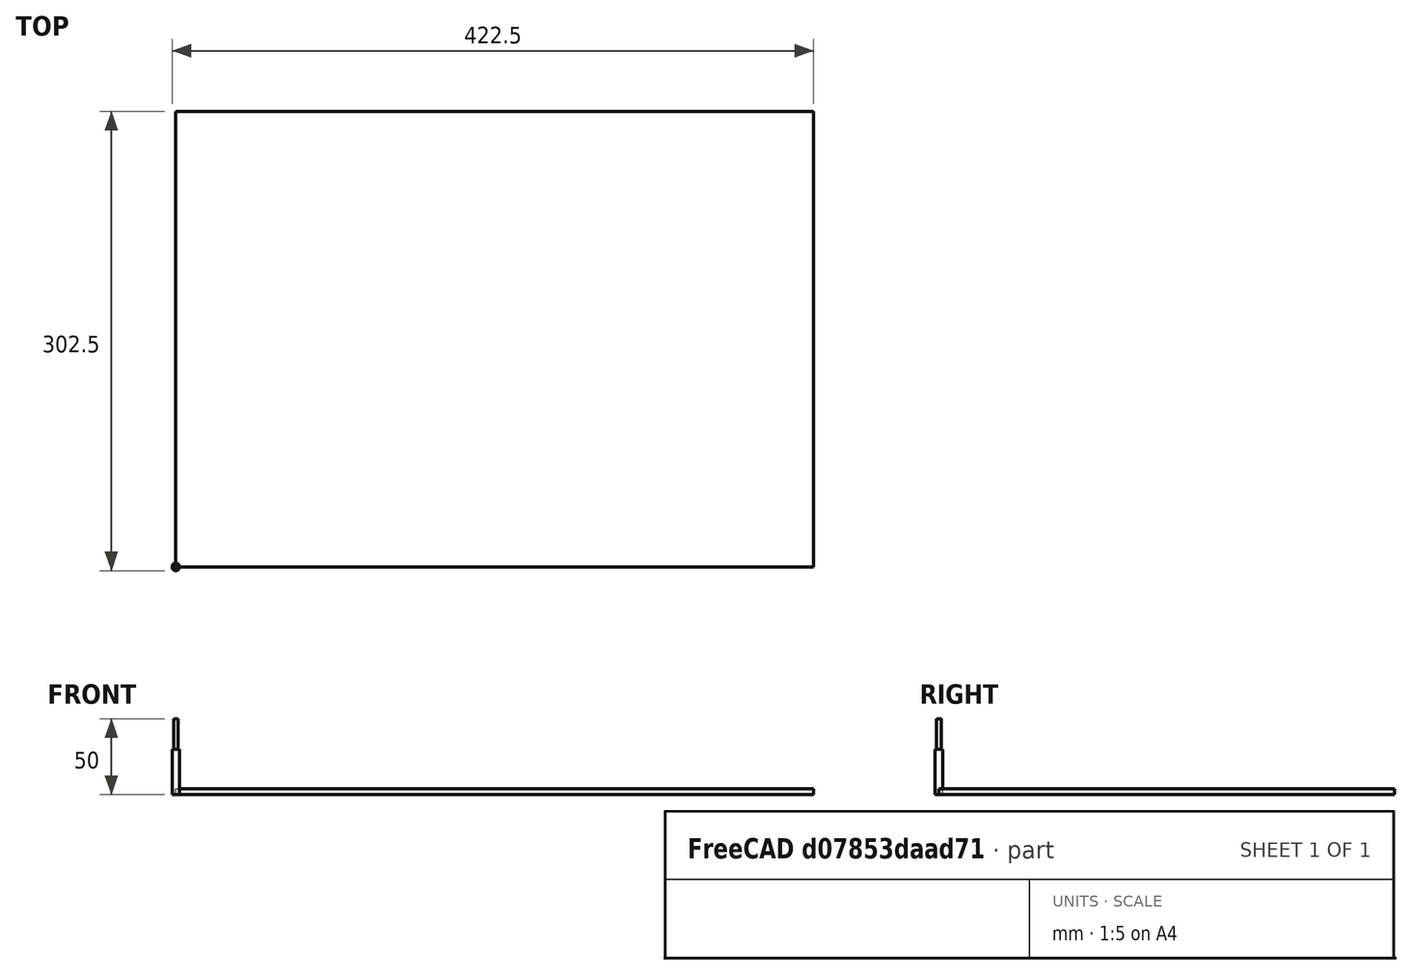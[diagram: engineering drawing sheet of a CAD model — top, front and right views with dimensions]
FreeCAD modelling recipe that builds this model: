
FCSTD DOCUMENT  (FreeCAD 1.0R39109 (Git))
Label: HousingAtari_T03.00
License: All rights reserved
LicenseURL: https://en.wikipedia.org/wiki/All_rights_reserved
objects: Sketcher::SketchObject×7, Part::Part2DObjectPython×5, Path::FeaturePython×3, App::DocumentObjectGroup×3, Part::FeaturePython×2, PartDesign::Body×1, App::FeaturePython×1, Mesh::FeaturePython×1
note: 22 computed .brp shape members not serialized (recipe doc carries the construction recipe); baked Part::Feature solids carry a one-line shape summary decoded from their .brp

FEATURE [Sketcher::SketchObject] Sketch  label="A3"
  ArcFitTolerance = 0
  FullyConstrained = false
  MakeInternals = false
  MapMode = 5
  sketch-geometry (7):
    g0: LineSegment StartX=0 StartY=420 StartZ=0 EndX=0 EndY=0 EndZ=0
    g1: LineSegment StartX=0 StartY=420 StartZ=0 EndX=148.5 EndY=420 EndZ=0
    g2: LineSegment StartX=148.5 StartY=420 StartZ=0 EndX=148.5 EndY=0 EndZ=0
    g3: LineSegment StartX=148.5 StartY=420 StartZ=0 EndX=297 EndY=420 EndZ=0
    g4: LineSegment StartX=297 StartY=420 StartZ=0 EndX=297 EndY=210 EndZ=0
    g5: LineSegment StartX=297 StartY=210 StartZ=0 EndX=297 EndY=0 EndZ=0
    g6: LineSegment StartX=297 StartY=210 StartZ=0 EndX=0 EndY=210 EndZ=0
  constraints (21):
    c: Vertical(g0)
    c: DistanceY(g0,g0) = 420
    c: Coincident(g1,g0)
    c: Horizontal(g1)
    c: Coincident(g2,g1)
    c: Coincident(g3,g1)
    c: Horizontal(g3)
    c: Equal(g1,g3)
    c: Vertical(g2)
    c: DistanceX(g0,g3) = 297
    c: Coincident(g4,g3)
    c: Vertical(g4)
    c: Coincident(g5,g4)
    c: PointOnObject(g5,g-1)
    c: Vertical(g5)
    c: Equal(g5,g4)
    c: PointOnObject(g0,g-1)
    c: PointOnObject(g0,g-2)
    c: Coincident(g6,g4)
    c: PointOnObject(g6,g0)
    c: Horizontal(g6)
FEATURE [Sketcher::SketchObject] Sketch001  label="BOX-OUTLINE"
  ArcFitTolerance = 0
  ExternalGeometry = -> [Sketch]
  FullyConstrained = false
  MakeInternals = false
  MapMode = 5
  sketch-geometry (60):
    g0: LineSegment StartX=83.5 StartY=362.836 StartZ=0 EndX=83.5 EndY=292.836 EndZ=0
    g1: LineSegment StartX=83.5 StartY=292.836 StartZ=0 EndX=83.5 EndY=222.836 EndZ=0
    g2: LineSegment StartX=83.5 StartY=222.836 StartZ=0 EndX=148.5 EndY=222.836 EndZ=0
    g3: LineSegment StartX=148.5 StartY=222.836 StartZ=0 EndX=213.5 EndY=222.836 EndZ=0
    g4: LineSegment StartX=213.5 StartY=222.836 StartZ=0 EndX=213.5 EndY=292.836 EndZ=0
    g5: LineSegment StartX=213.5 StartY=292.836 StartZ=0 EndX=213.5 EndY=362.836 EndZ=0
    g6: LineSegment StartX=213.5 StartY=362.836 StartZ=0 EndX=148.5 EndY=362.836 EndZ=0
    g7: LineSegment StartX=148.5 StartY=362.836 StartZ=0 EndX=83.5 EndY=362.836 EndZ=0
    g8: LineSegment StartX=83.5 StartY=222.836 StartZ=0 EndX=83.5 EndY=218.836 EndZ=0
    g9: LineSegment StartX=83.5 StartY=218.836 StartZ=0 EndX=213.5 EndY=218.836 EndZ=0
    g10: LineSegment StartX=213.5 StartY=218.836 StartZ=0 EndX=213.5 EndY=222.836 EndZ=0
    g11: LineSegment StartX=213.5 StartY=222.836 StartZ=0 EndX=217.5 EndY=222.836 EndZ=0
    g12: LineSegment StartX=217.5 StartY=222.836 StartZ=0 EndX=217.5 EndY=362.836 EndZ=0
    g13: LineSegment StartX=217.5 StartY=362.836 StartZ=0 EndX=213.5 EndY=362.836 EndZ=0
    g14: LineSegment StartX=213.5 StartY=362.836 StartZ=0 EndX=213.5 EndY=366.836 EndZ=0
    g15: LineSegment StartX=213.5 StartY=366.836 StartZ=0 EndX=83.5 EndY=366.836 EndZ=0
    g16: LineSegment StartX=83.5 StartY=366.836 StartZ=0 EndX=83.5 EndY=362.836 EndZ=0
    g17: LineSegment StartX=83.5 StartY=222.836 StartZ=0 EndX=79.5 EndY=222.836 EndZ=0
    g18: LineSegment StartX=79.5 StartY=222.836 StartZ=0 EndX=79.5 EndY=362.836 EndZ=0
    g19: LineSegment StartX=79.5 StartY=362.836 StartZ=0 EndX=83.5 EndY=362.836 EndZ=0
    g20: LineSegment StartX=83.5 StartY=218.836 StartZ=0 EndX=83.5 EndY=188.836 EndZ=0
    g21: LineSegment StartX=83.5 StartY=188.836 StartZ=0 EndX=213.5 EndY=188.836 EndZ=0
    g22: LineSegment StartX=213.5 StartY=188.836 StartZ=0 EndX=213.5 EndY=218.836 EndZ=0
    g23: LineSegment StartX=217.5 StartY=222.836 StartZ=0 EndX=243.5 EndY=222.836 EndZ=0
    g24: LineSegment StartX=243.5 StartY=222.836 StartZ=0 EndX=243.5 EndY=362.836 EndZ=0
    g25: LineSegment StartX=243.5 StartY=362.836 StartZ=0 EndX=217.5 EndY=362.836 EndZ=0
    g26: LineSegment StartX=213.5 StartY=366.836 StartZ=0 EndX=213.5 EndY=396.836 EndZ=0
    g27: LineSegment StartX=213.5 StartY=396.836 StartZ=0 EndX=83.5 EndY=396.836 EndZ=0
    g28: LineSegment StartX=83.5 StartY=396.836 StartZ=0 EndX=83.5 EndY=366.836 EndZ=0
    g29: LineSegment StartX=79.5 StartY=362.836 StartZ=0 EndX=53.5 EndY=362.836 EndZ=0
    g30: LineSegment StartX=53.5 StartY=362.836 StartZ=0 EndX=53.5 EndY=222.836 EndZ=0
    g31: LineSegment StartX=53.5 StartY=222.836 StartZ=0 EndX=79.5 EndY=222.836 EndZ=0
    g32: LineSegment StartX=213.5 StartY=188.836 StartZ=0 EndX=217.5 EndY=188.836 EndZ=0
    g33: LineSegment StartX=217.5 StartY=188.836 StartZ=0 EndX=217.5 EndY=222.836 EndZ=0
    g34: LineSegment StartX=213.5 StartY=218.836 StartZ=0 EndX=243.5 EndY=218.836 EndZ=0
    g35: LineSegment StartX=243.5 StartY=218.836 StartZ=0 EndX=243.5 EndY=222.836 EndZ=0
    g36: LineSegment StartX=213.5 StartY=366.836 StartZ=0 EndX=243.5 EndY=366.836 EndZ=0
    g37: LineSegment StartX=243.5 StartY=366.836 StartZ=0 EndX=243.5 EndY=362.836 EndZ=0
    g38: LineSegment StartX=217.5 StartY=362.836 StartZ=0 EndX=217.5 EndY=396.836 EndZ=0
    g39: LineSegment StartX=217.5 StartY=396.836 StartZ=0 EndX=213.5 EndY=396.836 EndZ=0
    g40: LineSegment StartX=83.5 StartY=396.836 StartZ=0 EndX=79.5 EndY=396.836 EndZ=0
    g41: LineSegment StartX=79.5 StartY=396.836 StartZ=0 EndX=79.5 EndY=362.836 EndZ=0
    g42: LineSegment StartX=53.5 StartY=362.836 StartZ=0 EndX=53.5 EndY=366.836 EndZ=0
    g43: LineSegment StartX=53.5 StartY=366.836 StartZ=0 EndX=83.5 EndY=366.836 EndZ=0
    g44: LineSegment StartX=53.5 StartY=222.836 StartZ=0 EndX=53.5 EndY=218.836 EndZ=0
    g45: LineSegment StartX=53.5 StartY=218.836 StartZ=0 EndX=83.5 EndY=218.836 EndZ=0
    g46: LineSegment StartX=79.5 StartY=222.836 StartZ=0 EndX=79.5 EndY=188.836 EndZ=0
    g47: LineSegment StartX=79.5 StartY=188.836 StartZ=0 EndX=83.5 EndY=188.836 EndZ=0
    g48: LineSegment StartX=83.5 StartY=188.836 StartZ=0 EndX=83.5 EndY=44.8363 EndZ=0
    g49: LineSegment StartX=83.5 StartY=44.8363 StartZ=0 EndX=213.5 EndY=44.8363 EndZ=0
    g50: LineSegment StartX=213.5 StartY=44.8363 StartZ=0 EndX=213.5 EndY=188.836 EndZ=0
    g51: LineSegment StartX=79.5 StartY=188.836 StartZ=0 EndX=79.5 EndY=48.8363 EndZ=0
    g52: LineSegment StartX=79.5 StartY=48.8363 StartZ=0 EndX=217.5 EndY=48.8363 EndZ=0
    g53: LineSegment StartX=217.5 StartY=48.8363 StartZ=0 EndX=217.5 EndY=188.836 EndZ=0
    g54: LineSegment StartX=79.5 StartY=192.836 StartZ=0 EndX=217.5 EndY=192.836 EndZ=0
    g55: LineSegment StartX=79.5 StartY=48.8363 StartZ=0 EndX=79.5 EndY=44.8363 EndZ=0
    g56: LineSegment StartX=217.5 StartY=48.8363 StartZ=0 EndX=217.5 EndY=44.8363 EndZ=0
    g57: LineSegment StartX=79.5 StartY=392.836 StartZ=0 EndX=217.5 EndY=392.836 EndZ=0
    g58: LineSegment StartX=247.5 StartY=366.836 StartZ=0 EndX=247.5 EndY=218.836 EndZ=0
    g59: LineSegment StartX=49.5 StartY=366.836 StartZ=0 EndX=49.5 EndY=218.836 EndZ=0
  constraints (166):
    c: Vertical(g0)
    c: Coincident(g1,g0)
    c: Vertical(g1)
    c: Coincident(g2,g1)
    c: Horizontal(g2)
    c: Coincident(g3,g2)
    c: Horizontal(g3)
    c: Coincident(g4,g3)
    c: Vertical(g4)
    c: Coincident(g5,g4)
    c: Vertical(g5)
    c: Horizontal(g6)
    c: Coincident(g7,g6)
    c: Coincident(g7,g0)
    c: Horizontal(g7)
    c: Vertical(g2,g6)
    c: Horizontal(g0,g4)
    c: Equal(g4,g5)
    c: Equal(g7,g6)
    c: Coincident(g5,g6)
    c: DistanceY(g1,g0) = 140
    c: DistanceX(g0,g5) = 130
    c: Coincident(g8,g1)
    c: Vertical(g8)
    c: Coincident(g9,g8)
    c: Horizontal(g9)
    c: Coincident(g10,g9)
    c: Coincident(g10,g3)
    c: Vertical(g10)
    c: Coincident(g11,g3)
    c: Horizontal(g11)
    c: Coincident(g12,g11)
    c: Vertical(g12)
    c: Coincident(g13,g12)
    c: Coincident(g13,g5)
    c: Horizontal(g13)
    c: Equal(g10,g11)
    c: DistanceY(g10,g10) = 4
    c: Coincident(g14,g5)
    c: Vertical(g14)
    c: Coincident(g15,g14)
    c: Horizontal(g15)
    c: Coincident(g16,g15)
    c: Coincident(g16,g0)
    c: Vertical(g16)
    c: Equal(g13,g14)
    c: Coincident(g17,g1)
    c: Horizontal(g17)
    c: Coincident(g18,g17)
    c: Vertical(g18)
    c: Coincident(g19,g18)
    c: Coincident(g19,g0)
    c: Horizontal(g19)
    c: Equal(g16,g19)
    c: Coincident(g20,g8)
    c: Vertical(g20)
    c: Coincident(g21,g20)
    c: Horizontal(g21)
    c: Coincident(g22,g21)
    c: Coincident(g22,g9)
    c: Coincident(g23,g11)
    c: Horizontal(g23)
    c: Coincident(g24,g23)
    c: Vertical(g24)
    c: Coincident(g25,g24)
    c: Coincident(g25,g12)
    c: Horizontal(g25)
    c: Coincident(g26,g14)
    c: Vertical(g26)
    c: Coincident(g27,g26)
    c: Horizontal(g27)
    c: Coincident(g28,g27)
    c: Coincident(g28,g15)
    c: Coincident(g29,g18)
    c: Horizontal(g29)
    c: Coincident(g30,g29)
    c: Vertical(g30)
    c: Coincident(g31,g30)
    c: Coincident(g31,g17)
    c: Horizontal(g31)
    c: Vertical(g22)
    c: Coincident(g32,g21)
    c: Horizontal(g32)
    c: Coincident(g33,g32)
    c: Coincident(g33,g11)
    c: Vertical(g33)
    c: Coincident(g34,g9)
    c: Horizontal(g34)
    c: Coincident(g35,g34)
    c: Coincident(g35,g23)
    c: Coincident(g36,g14)
    c: Horizontal(g36)
    c: Coincident(g37,g36)
    c: Coincident(g37,g24)
    c: Coincident(g38,g12)
    c: Vertical(g38)
    c: Coincident(g39,g38)
    c: Coincident(g39,g26)
    c: Horizontal(g39)
    c: Coincident(g40,g27)
    c: Horizontal(g40)
    c: Coincident(g41,g40)
    c: Coincident(g41,g18)
    c: Coincident(g42,g29)
    c: Vertical(g42)
    c: Coincident(g43,g42)
    c: Coincident(g43,g15)
    c: Coincident(g44,g30)
    c: Vertical(g44)
    c: Coincident(g45,g44)
    c: Coincident(g45,g8)
    c: Horizontal(g45)
    c: Coincident(g46,g17)
    c: Coincident(g47,g46)
    c: Coincident(g47,g20)
    c: Vertical(g37)
    c: Vertical(g46)
    c: Vertical(g35)
    c: Horizontal(g43)
    c: Horizontal(g47)
    c: DistanceY(g15,g27) = 30
    c: Vertical(g41)
    c: Vertical(g28)
    c: DistanceY(g22,g22) = 30
    c: Distance(g43,g43) = 30
    c: DistanceX(g34,g34) = 30
    c: Coincident(g48,g20)
    c: Vertical(g48)
    c: Coincident(g49,g48)
    c: Horizontal(g49)
    c: Coincident(g50,g49)
    c: Coincident(g50,g21)
    c: Vertical(g50)
    c: Coincident(g51,g46)
    c: Vertical(g51)
    c: Coincident(g52,g51)
    c: Horizontal(g52)
    c: Coincident(g53,g52)
    c: Coincident(g53,g32)
    c: Vertical(g53)
    c: PointOnObject(g54,g46)
    c: PointOnObject(g54,g33)
    c: Horizontal(g54)
    c: DistanceY(g46,g54) = 4
    c: Coincident(g55,g51)
    c: PointOnObject(g55,g49)
    c: Vertical(g55)
    c: DistanceY(g55,g55) = 4
    c: DistanceY(g51,g51) = 140
    c: DistanceY(g34,g36) = 148
    c: Coincident(g56,g52)
    c: PointOnObject(g56,g49)
    c: Vertical(g56)
    c: DistanceY(g56,g54) = 148
    c: PointOnObject(g57,g41)
    c: PointOnObject(g57,g38)
    c: Horizontal(g57)
    c: DistanceY(g57,g38) = 4
    c: PointOnObject(g6,g-3)
    c: PointOnObject(g58,g36)
    c: PointOnObject(g58,g34)
    c: Vertical(g58)
    c: PointOnObject(g59,g43)
    c: PointOnObject(g59,g45)
    c: Vertical(g59)
    c: DistanceX(g42,g59) = -4
FEATURE [PartDesign::Body] Body
  AllowCompound = false
  Group = -> [Sketch,Sketch001]
  Origin = -> Origin
FEATURE [Sketcher::SketchObject] Sketch002  label="CUT-BOX-BASE"
  ArcFitTolerance = 0
  ExternalGeometry = -> [Sketch001,Sketch]
  FullyConstrained = true
  MakeInternals = false
  MapMode = 5
  sketch-geometry (44):
    g0: LineSegment StartX=107.1 StartY=366.836 StartZ=0 EndX=79.5 EndY=366.836 EndZ=0
    g1: LineSegment StartX=189.9 StartY=366.836 StartZ=0 EndX=217.5 EndY=366.836 EndZ=0
    g2: LineSegment StartX=134.7 StartY=366.836 StartZ=0 EndX=162.3 EndY=366.836 EndZ=0
    g3: LineSegment StartX=162.3 StartY=362.836 StartZ=0 EndX=189.9 EndY=362.836 EndZ=0
    g4: LineSegment StartX=107.1 StartY=362.836 StartZ=0 EndX=134.7 EndY=362.836 EndZ=0
    g5: LineSegment StartX=107.1 StartY=366.836 StartZ=0 EndX=107.1 EndY=362.836 EndZ=0
    g6: LineSegment StartX=134.7 StartY=366.836 StartZ=0 EndX=134.7 EndY=362.836 EndZ=0
    g7: LineSegment StartX=162.3 StartY=366.836 StartZ=0 EndX=162.3 EndY=362.836 EndZ=0
    g8: LineSegment StartX=189.9 StartY=362.836 StartZ=0 EndX=189.9 EndY=366.836 EndZ=0
    g9: LineSegment [constr] StartX=107.1 StartY=362.836 StartZ=0 EndX=107.1 EndY=222.836 EndZ=0
    g10: LineSegment [constr] StartX=134.7 StartY=362.836 StartZ=0 EndX=134.7 EndY=222.836 EndZ=0
    g11: LineSegment [constr] StartX=162.3 StartY=362.836 StartZ=0 EndX=162.3 EndY=222.836 EndZ=0
    g12: LineSegment [constr] StartX=189.9 StartY=362.836 StartZ=0 EndX=189.9 EndY=222.836 EndZ=0
    g13: LineSegment StartX=79.5 StartY=218.836 StartZ=0 EndX=107.1 EndY=218.836 EndZ=0
    g14: LineSegment StartX=107.1 StartY=218.836 StartZ=0 EndX=107.1 EndY=222.836 EndZ=0
    g15: LineSegment StartX=107.1 StartY=222.836 StartZ=0 EndX=134.7 EndY=222.836 EndZ=0
    g16: LineSegment StartX=134.7 StartY=222.836 StartZ=0 EndX=134.7 EndY=218.836 EndZ=0
    g17: LineSegment StartX=134.7 StartY=218.836 StartZ=0 EndX=162.3 EndY=218.836 EndZ=0
    g18: LineSegment StartX=162.3 StartY=218.836 StartZ=0 EndX=162.3 EndY=222.836 EndZ=0
    g19: LineSegment StartX=162.3 StartY=222.836 StartZ=0 EndX=189.9 EndY=222.836 EndZ=0
    g20: LineSegment StartX=189.9 StartY=222.836 StartZ=0 EndX=189.9 EndY=218.836 EndZ=0
    g21: LineSegment StartX=189.9 StartY=218.836 StartZ=0 EndX=217.5 EndY=218.836 EndZ=0
    g22: LineSegment StartX=79.5 StartY=366.836 StartZ=0 EndX=79.5 EndY=336.163 EndZ=0
    g23: LineSegment StartX=79.5 StartY=305.49 StartZ=0 EndX=79.5 EndY=274.818 EndZ=0
    g24: LineSegment StartX=79.5 StartY=218.836 StartZ=0 EndX=79.5 EndY=244.145 EndZ=0
    g25: LineSegment StartX=79.5 StartY=336.163 StartZ=0 EndX=83.5 EndY=336.163 EndZ=0
    g26: LineSegment StartX=79.5 StartY=305.49 StartZ=0 EndX=83.5 EndY=305.49 EndZ=0
    g27: LineSegment StartX=79.5 StartY=274.818 StartZ=0 EndX=83.5 EndY=274.818 EndZ=0
    g28: LineSegment StartX=79.5 StartY=244.145 StartZ=0 EndX=83.5 EndY=244.145 EndZ=0
    g29: LineSegment StartX=83.5 StartY=305.49 StartZ=0 EndX=83.5 EndY=336.163 EndZ=0
    g30: LineSegment StartX=83.5 StartY=244.145 StartZ=0 EndX=83.5 EndY=274.818 EndZ=0
    g31: LineSegment [constr] StartX=83.5 StartY=336.163 StartZ=0 EndX=213.5 EndY=336.163 EndZ=0
    g32: LineSegment [constr] StartX=83.5 StartY=305.49 StartZ=0 EndX=213.5 EndY=305.49 EndZ=0
    g33: LineSegment [constr] StartX=83.5 StartY=274.818 StartZ=0 EndX=213.5 EndY=274.818 EndZ=0
    g34: LineSegment [constr] StartX=83.5 StartY=244.145 StartZ=0 EndX=213.5 EndY=244.145 EndZ=0
    g35: LineSegment StartX=217.5 StartY=366.836 StartZ=0 EndX=217.5 EndY=336.163 EndZ=0
    g36: LineSegment StartX=213.5 StartY=336.163 StartZ=0 EndX=217.5 EndY=336.163 EndZ=0
    g37: LineSegment StartX=213.5 StartY=305.49 StartZ=0 EndX=213.5 EndY=336.163 EndZ=0
    g38: LineSegment StartX=213.5 StartY=305.49 StartZ=0 EndX=217.5 EndY=305.49 EndZ=0
    g39: LineSegment StartX=213.5 StartY=274.818 StartZ=0 EndX=213.5 EndY=244.145 EndZ=0
    g40: LineSegment StartX=213.5 StartY=244.145 StartZ=0 EndX=217.5 EndY=244.145 EndZ=0
    g41: LineSegment StartX=217.5 StartY=244.145 StartZ=0 EndX=217.5 EndY=218.836 EndZ=0
    g42: LineSegment StartX=213.5 StartY=274.818 StartZ=0 EndX=217.5 EndY=274.818 EndZ=0
    g43: LineSegment StartX=217.5 StartY=274.818 StartZ=0 EndX=217.5 EndY=305.49 EndZ=0
  constraints (126):
    c: PointOnObject(g0,g-5)
    c: PointOnObject(g0,g-9)
    c: Horizontal(g0)
    c: PointOnObject(g1,g-5)
    c: PointOnObject(g1,g-10)
    c: Horizontal(g1)
    c: PointOnObject(g2,g-5)
    c: PointOnObject(g2,g-5)
    c: PointOnObject(g3,g-4)
    c: PointOnObject(g3,g-4)
    c: PointOnObject(g4,g-3)
    c: PointOnObject(g4,g-3)
    c: Coincident(g5,g0)
    c: Coincident(g5,g4)
    c: Coincident(g6,g2)
    c: Coincident(g6,g4)
    c: Coincident(g7,g2)
    c: Coincident(g7,g3)
    c: Coincident(g8,g3)
    c: Coincident(g8,g1)
    c: Vertical(g5)
    c: Vertical(g6)
    c: Vertical(g7)
    c: Vertical(g8)
    c: Equal(g0,g1)
    c: Equal(g4,g2)
    c: Equal(g3,g2)
    c: Equal(g0,g2)
    c: Coincident(g9,g4)
    c: PointOnObject(g9,g-6)
    c: Vertical(g9)
    c: Coincident(g10,g4)
    c: PointOnObject(g10,g-6)
    c: Vertical(g10)
    c: Coincident(g11,g3)
    c: PointOnObject(g11,g-8)
    c: Vertical(g11)
    c: Coincident(g12,g3)
    c: PointOnObject(g12,g-8)
    c: Vertical(g12)
    c: PointOnObject(g13,g-12)
    c: PointOnObject(g13,g-7)
    c: Horizontal(g13)
    c: Coincident(g14,g13)
    c: Coincident(g14,g9)
    c: Coincident(g15,g9)
    c: Coincident(g15,g10)
    c: Coincident(g16,g10)
    c: PointOnObject(g16,g-7)
    c: Coincident(g17,g16)
    c: PointOnObject(g17,g-7)
    c: Coincident(g18,g17)
    c: Coincident(g18,g11)
    c: Coincident(g19,g11)
    c: Coincident(g19,g12)
    c: Coincident(g20,g12)
    c: PointOnObject(g20,g-7)
    c: Vertical(g20)
    c: Coincident(g21,g20)
    c: PointOnObject(g21,g-11)
    c: Horizontal(g21)
    c: Vertical(g14)
    c: Vertical(g16)
    c: Vertical(g18)
    c: DistanceY(g21,g1) = 148
    c: DistanceX(g0,g1) = 138
    c: Coincident(g22,g0)
    c: PointOnObject(g22,g-14)
    c: PointOnObject(g23,g-14)
    c: PointOnObject(g23,g-14)
    c: Coincident(g24,g13)
    c: PointOnObject(g24,g-14)
    c: Coincident(g25,g22)
    c: PointOnObject(g25,g-16)
    c: Horizontal(g25)
    c: Coincident(g26,g23)
    c: PointOnObject(g26,g-16)
    c: Horizontal(g26)
    c: Coincident(g27,g23)
    c: PointOnObject(g27,g-17)
    c: Coincident(g28,g24)
    c: PointOnObject(g28,g-17)
    c: Horizontal(g28)
    c: Horizontal(g27)
    c: Equal(g22,g23)
    c: Coincident(g29,g26)
    c: Coincident(g29,g25)
    c: Coincident(g30,g28)
    c: Coincident(g30,g27)
    c: Equal(g30,g23)
    c: Equal(g29,g30)
    c: Equal(g29,g22)
    c: Coincident(g31,g25)
    c: PointOnObject(g31,g-18)
    c: Horizontal(g31)
    c: Coincident(g32,g26)
    c: PointOnObject(g32,g-18)
    c: Horizontal(g32)
    c: Coincident(g33,g27)
    c: PointOnObject(g33,g-19)
    c: Horizontal(g33)
    c: Coincident(g34,g28)
    c: PointOnObject(g34,g-19)
    c: Horizontal(g34)
    c: Coincident(g35,g1)
    c: PointOnObject(g35,g-15)
    c: Coincident(g36,g31)
    c: Coincident(g36,g35)
    c: Coincident(g37,g32)
    c: Coincident(g37,g31)
    c: Coincident(g38,g32)
    c: PointOnObject(g38,g-15)
    c: Coincident(g39,g33)
    c: Coincident(g39,g34)
    c: Coincident(g40,g34)
    c: PointOnObject(g40,g-15)
    c: Coincident(g41,g40)
    c: Coincident(g41,g21)
    c: Horizontal(g36)
    c: Horizontal(g38)
    c: Horizontal(g40)
    c: Coincident(g42,g33)
    c: PointOnObject(g42,g-15)
    c: Horizontal(g42)
    c: Coincident(g43,g42)
    c: Coincident(g43,g38)
FEATURE [Sketcher::SketchObject] Sketch003  label="CUT-Functional"
  ArcFitTolerance = 0
  ExternalGeometry = -> [Sketch]
  FullyConstrained = false
  MakeInternals = false
  MapMode = 5
  sketch-geometry (36):
    g0: LineSegment [constr] StartX=118.5 StartY=350.114 StartZ=0 EndX=148.5 EndY=350.114 EndZ=0
    g1: LineSegment [constr] StartX=148.5 StartY=350.114 StartZ=0 EndX=178.5 EndY=350.114 EndZ=0
    g2: Circle CenterX=118.5 CenterY=350.114 CenterZ=0 NormalX=0 NormalY=0 NormalZ=1 AngleXU=0 Radius=8
    g3: Circle CenterX=148.5 CenterY=350.114 CenterZ=0 NormalX=0 NormalY=0 NormalZ=1 AngleXU=0 Radius=8
    g4: Circle CenterX=178.5 CenterY=350.114 CenterZ=0 NormalX=0 NormalY=0 NormalZ=1 AngleXU=0 Radius=8
    g5: Circle CenterX=163.5 CenterY=331.863 CenterZ=0 NormalX=0 NormalY=0 NormalZ=1 AngleXU=0 Radius=8
    g6: Circle CenterX=133.5 CenterY=331.863 CenterZ=0 NormalX=0 NormalY=0 NormalZ=1 AngleXU=0 Radius=8
    g7: LineSegment [constr] StartX=133.5 StartY=331.863 StartZ=0 EndX=163.5 EndY=331.863 EndZ=0
    g8: LineSegment [constr] StartX=133.5 StartY=331.863 StartZ=0 EndX=118.5 EndY=350.114 EndZ=0
    g9: LineSegment [constr] StartX=163.5 StartY=331.863 StartZ=0 EndX=178.5 EndY=350.114 EndZ=0
    g10: LineSegment StartX=136 StartY=316.42 StartZ=0 EndX=136 EndY=306.42 EndZ=0
    g11: LineSegment StartX=136 StartY=306.42 StartZ=0 EndX=161 EndY=306.42 EndZ=0
    g12: LineSegment StartX=161 StartY=306.42 StartZ=0 EndX=161 EndY=316.42 EndZ=0
    g13: LineSegment StartX=136 StartY=316.42 StartZ=0 EndX=148.5 EndY=316.42 EndZ=0
    g14: LineSegment StartX=161 StartY=316.42 StartZ=0 EndX=148.5 EndY=316.42 EndZ=0
    g15: ArcOfCircle CenterX=230.249 CenterY=259.609 CenterZ=0 NormalX=0 NormalY=0 NormalZ=1 AngleXU=0 Radius=5 StartAngle=-1.05604e-11 EndAngle=3.14159
    g16: ArcOfCircle CenterX=230.249 CenterY=239.609 CenterZ=0 NormalX=0 NormalY=0 NormalZ=1 AngleXU=0 Radius=5 StartAngle=3.14159 EndAngle=6.28319
    g17: LineSegment StartX=235.249 StartY=259.609 StartZ=0 EndX=235.249 EndY=239.609 EndZ=0
    g18: LineSegment StartX=225.249 StartY=259.609 StartZ=0 EndX=225.249 EndY=239.609 EndZ=0
    g19: LineSegment [constr] StartX=67.0736 StartY=260.219 StartZ=0 EndX=67.0736 EndY=247.719 EndZ=0
    g20: LineSegment [constr] StartX=67.0736 StartY=247.719 StartZ=0 EndX=67.0736 EndY=235.219 EndZ=0
    g21: Circle CenterX=67.0736 CenterY=235.219 CenterZ=0 NormalX=0 NormalY=0 NormalZ=1 AngleXU=0 Radius=2
    g22: Circle CenterX=67.0736 CenterY=260.219 CenterZ=0 NormalX=0 NormalY=0 NormalZ=1 AngleXU=0 Radius=2
    g23: LineSegment [constr] StartX=67.0736 StartY=247.719 StartZ=0 EndX=70.7296 EndY=247.719 EndZ=0
    g24: LineSegment [constr] StartX=70.7296 StartY=247.719 StartZ=0 EndX=70.7296 EndY=255.982 EndZ=0
    g25: LineSegment [constr] StartX=70.7296 StartY=255.982 StartZ=0 EndX=62.7211 EndY=255.982 EndZ=0
    g26: LineSegment [constr] StartX=62.7211 StartY=255.982 StartZ=0 EndX=62.7211 EndY=247.719 EndZ=0
    g27: LineSegment [constr] StartX=62.7211 StartY=247.719 StartZ=0 EndX=67.0736 EndY=247.719 EndZ=0
    g28: LineSegment [constr] StartX=62.7296 StartY=238.982 StartZ=0 EndX=70.7296 EndY=238.982 EndZ=0
    g29: LineSegment [constr] StartX=70.7296 StartY=238.982 StartZ=0 EndX=70.7296 EndY=247.719 EndZ=0
    g30: LineSegment [constr] StartX=62.7296 StartY=255.995 StartZ=0 EndX=62.7211 EndY=238.995 EndZ=0
    g31: LineSegment StartX=62.7296 StartY=255.995 StartZ=0 EndX=62.7296 EndY=238.982 EndZ=0
    g32: LineSegment StartX=62.7296 StartY=239.09 StartZ=0 EndX=70.7296 EndY=240.829 EndZ=0
    g33: LineSegment StartX=70.7296 StartY=254.608 StartZ=0 EndX=62.9407 EndY=255.982 EndZ=0
    g34: LineSegment StartX=70.7296 StartY=240.829 StartZ=0 EndX=70.7296 EndY=247.719 EndZ=0
    g35: LineSegment StartX=70.7296 StartY=247.719 StartZ=0 EndX=70.7296 EndY=254.608 EndZ=0
  constraints (84):
    c: Horizontal(g0)
    c: Coincident(g1,g0)
    c: Horizontal(g1)
    c: Equal(g1,g0)
    c: Coincident(g2,g0)
    c: Coincident(g3,g0)
    c: Coincident(g4,g1)
    c: Equal(g4,g3)
    c: Equal(g3,g2)
    c: Diameter(g4) = 16
    c: DistanceX(g1,g1) = 30
    c: Coincident(g7,g6)
    c: Coincident(g7,g5)
    c: Equal(g1,g7)
    c: Horizontal(g7)
    c: Coincident(g8,g6)
    c: Coincident(g8,g0)
    c: Coincident(g9,g5)
    c: Coincident(g9,g1)
    c: Equal(g9,g8)
    c: Equal(g4,g5)
    c: Equal(g5,g6)
    c: Coincident(g10,g11)
    c: Coincident(g11,g12)
    c: Vertical(g10)
    c: Vertical(g12)
    c: Horizontal(g11)
    c: Coincident(g13,g10)
    c: PointOnObject(g13,g-3)
    c: Horizontal(g13)
    c: Coincident(g14,g12)
    c: Coincident(g14,g13)
    c: Horizontal(g14)
    c: Equal(g14,g13)
    c: DistanceX(g11,g11) = 25
    c: DistanceY(g12,g12) = 10
    c: PointOnObject(g0,g-3)
    c: Tangent(g15,g17) = 1.5708
    c: Tangent(g15,g18) = -1.5708
    c: Tangent(g16,g17) = 1.5708
    c: Tangent(g16,g18) = -1.5708
    c: Equal(g15,g16)
    c: Vertical(g18)
    c: DistanceX(g15,g15) = 10
    c: DistanceY(g17,g17) = 20
    c: Vertical(g19)
    c: Coincident(g20,g19)
    c: Vertical(g20)
    c: Coincident(g21,g20)
    c: Coincident(g22,g19)
    c: Equal(g22,g21)
    c: Diameter(g22) = 4
    c: Coincident(g23,g19)
    c: Horizontal(g23)
    c: Coincident(g24,g23)
    c: Vertical(g24)
    c: Coincident(g25,g24)
    c: Horizontal(g25)
    c: Coincident(g26,g25)
    c: Vertical(g26)
    c: Coincident(g27,g26)
    c: Coincident(g27,g19)
    c: Horizontal(g27)
    c: Horizontal(g28)
    c: Coincident(g29,g28)
    c: Coincident(g29,g23)
    c: Vertical(g29)
    c: DistanceY(g28,g25) = 17
    c: Equal(g19,g20)
    c: DistanceY(g20,g19) = 25
    c: DistanceX(g28,g28) = 8
    c: Coincident(g31,g30)
    c: Coincident(g31,g28)
    c: Vertical(g31)
    c: PointOnObject(g32,g31)
    c: PointOnObject(g32,g29)
    c: PointOnObject(g33,g24)
    c: PointOnObject(g33,g25)
    c: Angle(g33,g25) = 0.174533
    c: Coincident(g34,g32)
    c: Coincident(g34,g23)
    c: Coincident(g35,g23)
    c: Coincident(g35,g33)
    c: Equal(g35,g34)
FEATURE [App::FeaturePython] SetupSheet  # Path/CAM operation (typed FeaturePython)
  ClearanceHeightExpression = OpStockZMax+SetupSheet.ClearanceHeightOffset
  ClearanceHeightOffset = 5
  CoolantMode = 0
  CoolantModes = None | Flood | Mist
  FinalDepthExpression = OpFinalDepth
  HorizRapid = 0
  SafeHeightExpression = OpStockZMax+SetupSheet.SafeHeightOffset
  SafeHeightOffset = 3
  StartDepthExpression = OpStartDepth
  StepDownExpression = OpToolDiameter
  VertRapid = 0
FEATURE [Part::Part2DObjectPython] Clone2D  label="Model-CUT-BOX"  # Draft 2D object (typed FeaturePython)
  Fuse = false
  Objects = -> [Sketch002]
  PathResource = Model
  Scale = (1,1,1)
FEATURE [Part::Part2DObjectPython] Clone2D001  label="Model-CUT-Functional"  # Draft 2D object (typed FeaturePython)
  Fuse = false
  Objects = -> [Sketch003]
  PathResource = Model
  Scale = (1,1,1)
FEATURE [Part::FeaturePython] ToolBit  label="Endmill"  # Path/CAM toolbit (typed FeaturePython)
  BitPropertyNames = Chipload | CuttingEdgeHeight | Diameter | Flutes | Length | Material | ShankDiameter | SpindleDirection
  BitShape = <path>
  Chipload = 0
  CuttingEdgeHeight = 30
  Diameter = 5
  Flutes = 0
  Length = 50
  Material = 0
  ShankDiameter = 3
  ShapeName = endmill
  SpindleDirection = 0
FEATURE [Path::FeaturePython] TC__Default_Tool  label="TC: Default Tool"  # Path/CAM operation (typed FeaturePython)
  HorizFeed = 1000
  HorizRapid = 1000
  SpindleDir = 0
  SpindleSpeed = 1000
  Tool = -> ToolBit
  ToolNumber = 1
  VertFeed = 1000
  VertRapid = 1000
  expr: HorizRapid = 1000
  expr: VertRapid = 1000
FEATURE [App::DocumentObjectGroup] Tools
  Group = -> [TC__Default_Tool]
FEATURE [Path::FeaturePython] Engrave  # Path/CAM operation (typed FeaturePython)
  Active = true
  ClearanceHeight = 9
  CoolantMode = 0
  CycleTime = 00:00:04
  FinalDepth = -5
  OpFinalDepth = -5
  OpStartDepth = 0
  OpStockZMax = 4
  OpStockZMin = 0
  OpToolDiameter = 5
  SafeHeight = 7
  StartDepth = 0
  StartVertex = 0
  StepDown = 5
  ToolController = -> TC__Default_Tool
  expr: ClearanceHeight = OpStockZMax + SetupSheet.ClearanceHeightOffset
  expr: FinalDepth = OpFinalDepth
  expr: SafeHeight = OpStockZMax + SetupSheet.SafeHeightOffset
  expr: StartDepth = OpStartDepth
  expr: StepDown = OpToolDiameter
FEATURE [App::DocumentObjectGroup] Operations
  Group = -> [Engrave]
FEATURE [Part::FeaturePython] Stock001  # WARN: FeaturePython — macro-defined, semantics opaque (R4)
  Height = 4
  Length = 420
  StockType = CreateBox
  Width = 300
FEATURE [Mesh::FeaturePython] CutMaterial  # WARN: FeaturePython — macro-defined, semantics opaque (R4)
FEATURE [Sketcher::SketchObject] Sketch004  label="CUT-BOX-WALLS"
  ArcFitTolerance = 0
  ExternalGeometry = -> [Sketch001,Sketch002]
  FullyConstrained = false
  MakeInternals = false
  MapMode = 5
  sketch-geometry (99):
    g0: LineSegment [constr] StartX=107.1 StartY=366.836 StartZ=0 EndX=107.1 EndY=396.836 EndZ=0
    g1: LineSegment [constr] StartX=134.7 StartY=366.836 StartZ=0 EndX=134.7 EndY=396.836 EndZ=0
    g2: LineSegment [constr] StartX=162.3 StartY=366.836 StartZ=0 EndX=162.3 EndY=396.836 EndZ=0
    g3: LineSegment [constr] StartX=189.9 StartY=366.836 StartZ=0 EndX=189.9 EndY=396.836 EndZ=0
    g4: LineSegment StartX=79.5 StartY=366.836 StartZ=0 EndX=79.5 EndY=376.836 EndZ=0
    g5: LineSegment StartX=79.5 StartY=376.836 StartZ=0 EndX=83.5 EndY=376.836 EndZ=0
    g6: LineSegment StartX=83.5 StartY=376.836 StartZ=0 EndX=83.5 EndY=386.836 EndZ=0
    g7: LineSegment StartX=83.5 StartY=386.836 StartZ=0 EndX=79.5 EndY=386.836 EndZ=0
    g8: LineSegment StartX=79.5 StartY=386.836 StartZ=0 EndX=79.5 EndY=396.836 EndZ=0
    g9: LineSegment StartX=79.5 StartY=362.836 StartZ=0 EndX=69.5 EndY=362.836 EndZ=0
    g10: LineSegment StartX=69.5 StartY=362.836 StartZ=0 EndX=69.5 EndY=366.836 EndZ=0
    g11: LineSegment StartX=69.5 StartY=366.836 StartZ=0 EndX=59.5 EndY=366.836 EndZ=0
    g12: LineSegment StartX=59.5 StartY=366.836 StartZ=0 EndX=59.5 EndY=362.815 EndZ=0
    g13: LineSegment StartX=59.5 StartY=362.815 StartZ=0 EndX=49.5 EndY=362.815 EndZ=0
    g14: LineSegment [constr] StartX=83.5 StartY=386.836 StartZ=0 EndX=217.5 EndY=386.836 EndZ=0
    g15: LineSegment [constr] StartX=83.5 StartY=376.836 StartZ=0 EndX=217.5 EndY=376.836 EndZ=0
    g16: LineSegment [constr] StartX=189.9 StartY=366.836 StartZ=0 EndX=189.9 EndY=396.836 EndZ=0
    g17: LineSegment StartX=217.5 StartY=366.836 StartZ=0 EndX=217.5 EndY=376.836 EndZ=0
    g18: LineSegment StartX=217.5 StartY=376.836 StartZ=0 EndX=213.5 EndY=376.836 EndZ=0
    g19: LineSegment StartX=213.5 StartY=376.836 StartZ=0 EndX=213.5 EndY=386.836 EndZ=0
    g20: LineSegment StartX=213.5 StartY=386.836 StartZ=0 EndX=217.5 EndY=386.836 EndZ=0
    g21: LineSegment StartX=217.5 StartY=386.836 StartZ=0 EndX=217.5 EndY=396.836 EndZ=0
    g22: LineSegment StartX=227.5 StartY=366.836 StartZ=0 EndX=237.5 EndY=366.836 EndZ=0
    g23: LineSegment StartX=237.5 StartY=366.836 StartZ=0 EndX=237.5 EndY=362.836 EndZ=0
    g24: LineSegment StartX=237.5 StartY=362.836 StartZ=0 EndX=247.5 EndY=362.836 EndZ=0
    g25: LineSegment StartX=217.5 StartY=362.836 StartZ=0 EndX=227.5 EndY=362.836 EndZ=0
    g26: LineSegment StartX=227.5 StartY=362.836 StartZ=0 EndX=227.5 EndY=366.836 EndZ=0
    g27: LineSegment [constr] StartX=59.5 StartY=362.815 StartZ=0 EndX=59.5 EndY=218.836 EndZ=0
    g28: LineSegment [constr] StartX=69.5 StartY=218.836 StartZ=0 EndX=69.5 EndY=362.836 EndZ=0
    g29: LineSegment [constr] StartX=227.5 StartY=362.836 StartZ=0 EndX=227.5 EndY=218.836 EndZ=0
    g30: LineSegment [constr] StartX=237.5 StartY=362.836 StartZ=0 EndX=237.5 EndY=218.836 EndZ=0
    g31: LineSegment StartX=79.5 StartY=222.836 StartZ=0 EndX=69.5 EndY=222.836 EndZ=0
    g32: LineSegment StartX=69.5 StartY=222.836 StartZ=0 EndX=69.5 EndY=218.836 EndZ=0
    g33: LineSegment StartX=69.5 StartY=218.836 StartZ=0 EndX=59.5 EndY=218.836 EndZ=0
    g34: LineSegment StartX=59.5 StartY=222.836 StartZ=0 EndX=59.5 EndY=218.836 EndZ=0
    g35: LineSegment StartX=59.5 StartY=222.836 StartZ=0 EndX=49.5 EndY=222.836 EndZ=0
    g36: LineSegment StartX=217.5 StartY=222.836 StartZ=0 EndX=227.5 EndY=222.836 EndZ=0
    g37: LineSegment StartX=227.5 StartY=222.836 StartZ=0 EndX=227.5 EndY=218.836 EndZ=0
    g38: LineSegment StartX=227.5 StartY=218.836 StartZ=0 EndX=237.5 EndY=218.836 EndZ=0
    g39: LineSegment StartX=247.5 StartY=222.836 StartZ=0 EndX=237.5 EndY=222.836 EndZ=0
    g40: LineSegment StartX=237.5 StartY=222.836 StartZ=0 EndX=237.5 EndY=218.836 EndZ=0
    g41: LineSegment StartX=79.5 StartY=218.836 StartZ=0 EndX=79.5 EndY=208.836 EndZ=0
    g42: LineSegment StartX=79.5 StartY=208.836 StartZ=0 EndX=83.5 EndY=208.836 EndZ=0
    g43: LineSegment StartX=83.5 StartY=208.836 StartZ=0 EndX=83.5 EndY=198.836 EndZ=0
    g44: LineSegment StartX=83.5 StartY=198.836 StartZ=0 EndX=79.5 EndY=198.836 EndZ=0
    g45: LineSegment StartX=79.5 StartY=198.836 StartZ=0 EndX=79.5 EndY=188.836 EndZ=0
    g46: LineSegment [constr] StartX=83.5 StartY=208.836 StartZ=0 EndX=213.5 EndY=208.836 EndZ=0
    g47: LineSegment [constr] StartX=83.5 StartY=198.836 StartZ=0 EndX=213.5 EndY=198.836 EndZ=0
    g48: LineSegment StartX=217.5 StartY=218.836 StartZ=0 EndX=217.5 EndY=208.836 EndZ=0
    g49: LineSegment StartX=217.5 StartY=208.836 StartZ=0 EndX=213.5 EndY=208.836 EndZ=0
    g50: LineSegment StartX=213.5 StartY=208.836 StartZ=0 EndX=213.5 EndY=198.836 EndZ=0
    g51: LineSegment StartX=213.5 StartY=198.836 StartZ=0 EndX=217.5 EndY=198.836 EndZ=0
    g52: LineSegment StartX=217.5 StartY=198.836 StartZ=0 EndX=217.5 EndY=188.836 EndZ=0
    g53: LineSegment [constr] StartX=49.5 StartY=336.163 StartZ=0 EndX=247.5 EndY=336.163 EndZ=0
    g54: LineSegment [constr] StartX=49.5 StartY=305.49 StartZ=0 EndX=247.5 EndY=305.49 EndZ=0
    g55: LineSegment [constr] StartX=49.5 StartY=274.818 StartZ=0 EndX=247.5 EndY=274.818 EndZ=0
    g56: LineSegment [constr] StartX=49.5 StartY=244.145 StartZ=0 EndX=247.5 EndY=244.145 EndZ=0
    g57: LineSegment [constr] StartX=107.1 StartY=396.836 StartZ=0 EndX=107.1 EndY=392.836 EndZ=0
    g58: LineSegment StartX=79.5 StartY=396.836 StartZ=0 EndX=107.1 EndY=396.836 EndZ=0
    g59: LineSegment StartX=107.1 StartY=392.836 StartZ=0 EndX=107.1 EndY=396.836 EndZ=0
    g60: LineSegment StartX=107.1 StartY=392.836 StartZ=0 EndX=134.7 EndY=392.836 EndZ=0
    g61: LineSegment StartX=134.7 StartY=392.836 StartZ=0 EndX=134.7 EndY=396.836 EndZ=0
    g62: LineSegment StartX=134.7 StartY=396.836 StartZ=0 EndX=162.3 EndY=396.836 EndZ=0
    g63: LineSegment StartX=162.3 StartY=396.836 StartZ=0 EndX=162.3 EndY=392.836 EndZ=0
    g64: LineSegment StartX=162.3 StartY=392.836 StartZ=0 EndX=189.9 EndY=392.836 EndZ=0
    g65: LineSegment StartX=189.9 StartY=392.836 StartZ=0 EndX=189.9 EndY=396.836 EndZ=0
    g66: LineSegment StartX=189.9 StartY=396.836 StartZ=0 EndX=217.5 EndY=396.836 EndZ=0
    g67: LineSegment [constr] StartX=107.1 StartY=362.836 StartZ=0 EndX=107.1 EndY=188.836 EndZ=0
    g68: LineSegment [constr] StartX=134.7 StartY=362.836 StartZ=0 EndX=134.7 EndY=188.836 EndZ=0
    g69: LineSegment [constr] StartX=162.3 StartY=362.836 StartZ=0 EndX=162.3 EndY=188.836 EndZ=0
    g70: LineSegment [constr] StartX=189.9 StartY=362.836 StartZ=0 EndX=189.9 EndY=188.836 EndZ=0
    g71: LineSegment StartX=79.5 StartY=188.836 StartZ=0 EndX=107.1 EndY=188.836 EndZ=0
    g72: LineSegment StartX=134.7 StartY=188.836 StartZ=0 EndX=162.3 EndY=188.836 EndZ=0
    g73: LineSegment StartX=189.9 StartY=188.836 StartZ=0 EndX=217.5 EndY=188.836 EndZ=0
    g74: LineSegment [constr] StartX=107.1 StartY=188.836 StartZ=0 EndX=107.1 EndY=192.836 EndZ=0
    g75: LineSegment StartX=107.1 StartY=188.836 StartZ=0 EndX=107.1 EndY=192.836 EndZ=0
    g76: LineSegment StartX=107.1 StartY=192.836 StartZ=0 EndX=134.7 EndY=192.836 EndZ=0
    g77: LineSegment StartX=134.7 StartY=192.836 StartZ=0 EndX=134.7 EndY=188.836 EndZ=0
    g78: LineSegment StartX=162.3 StartY=188.836 StartZ=0 EndX=162.3 EndY=192.836 EndZ=0
    g79: LineSegment StartX=162.3 StartY=192.836 StartZ=0 EndX=189.9 EndY=192.836 EndZ=0
    g80: LineSegment StartX=189.9 StartY=192.836 StartZ=0 EndX=189.9 EndY=188.836 EndZ=0
    g81: LineSegment StartX=49.5 StartY=222.836 StartZ=0 EndX=49.5 EndY=244.145 EndZ=0
    g82: LineSegment StartX=49.5 StartY=244.145 StartZ=0 EndX=53.5 EndY=244.145 EndZ=0
    g83: LineSegment StartX=53.5 StartY=244.145 StartZ=0 EndX=53.5 EndY=274.818 EndZ=0
    g84: LineSegment StartX=53.5 StartY=274.818 StartZ=0 EndX=49.5 EndY=274.818 EndZ=0
    g85: LineSegment StartX=49.5 StartY=274.818 StartZ=0 EndX=49.5 EndY=305.49 EndZ=0
    g86: LineSegment StartX=49.5 StartY=305.49 StartZ=0 EndX=53.5 EndY=305.49 EndZ=0
    g87: LineSegment StartX=53.5 StartY=305.49 StartZ=0 EndX=53.5 EndY=336.163 EndZ=0
    g88: LineSegment StartX=53.5 StartY=336.163 StartZ=0 EndX=49.5 EndY=336.163 EndZ=0
    g89: LineSegment StartX=49.5 StartY=336.163 StartZ=0 EndX=49.5 EndY=362.815 EndZ=0
    g90: LineSegment StartX=247.5 StartY=222.836 StartZ=0 EndX=247.5 EndY=244.145 EndZ=0
    g91: LineSegment StartX=247.5 StartY=244.145 StartZ=0 EndX=243.5 EndY=244.145 EndZ=0
    g92: LineSegment StartX=243.5 StartY=244.145 StartZ=0 EndX=243.5 EndY=274.818 EndZ=0
    g93: LineSegment StartX=243.5 StartY=274.818 StartZ=0 EndX=247.5 EndY=274.818 EndZ=0
    g94: LineSegment StartX=247.5 StartY=274.818 StartZ=0 EndX=247.5 EndY=305.49 EndZ=0
    g95: LineSegment StartX=247.5 StartY=362.836 StartZ=0 EndX=247.5 EndY=336.163 EndZ=0
    g96: LineSegment StartX=247.5 StartY=336.163 StartZ=0 EndX=243.5 EndY=336.163 EndZ=0
    g97: LineSegment StartX=243.5 StartY=336.163 StartZ=0 EndX=243.5 EndY=305.329 EndZ=0
    g98: LineSegment StartX=243.5 StartY=305.329 StartZ=0 EndX=247.5 EndY=305.49 EndZ=0
  constraints (273):
    c: Coincident(g0,g-18)
    c: PointOnObject(g0,g-22)
    c: Vertical(g0)
    c: Coincident(g1,g-17)
    c: PointOnObject(g1,g-22)
    c: Vertical(g1)
    c: Coincident(g2,g-16)
    c: PointOnObject(g2,g-22)
    c: Vertical(g2)
    c: Coincident(g3,g-15)
    c: PointOnObject(g3,g-22)
    c: Vertical(g3)
    c: PointOnObject(g4,g-27)
    c: PointOnObject(g4,g-27)
    c: Coincident(g5,g4)
    c: PointOnObject(g5,g-31)
    c: Horizontal(g5)
    c: Coincident(g6,g5)
    c: PointOnObject(g6,g-31)
    c: Coincident(g7,g6)
    c: PointOnObject(g7,g-27)
    c: Horizontal(g7)
    c: Coincident(g8,g7)
    c: Coincident(g8,g-27)
    c: Equal(g4,g6)
    c: Equal(g6,g8)
    c: PointOnObject(g4,g-23)
    c: Coincident(g9,g-27)
    c: Horizontal(g9)
    c: Coincident(g10,g9)
    c: PointOnObject(g10,g-23)
    c: Vertical(g10)
    c: Coincident(g11,g10)
    c: PointOnObject(g11,g-23)
    c: Coincident(g12,g11)
    c: Vertical(g12)
    c: Equal(g9,g4)
    c: Equal(g11,g6)
    c: DistanceY(g0,g0) = 30
    c: DistanceX(g-32,g-3) = 30
    c: Coincident(g13,g12)
    c: PointOnObject(g13,g-32)
    c: Horizontal(g13)
    c: Equal(g13,g11)
    c: DistanceY(g-29,g-33) = 30
    c: Coincident(g14,g6)
    c: PointOnObject(g14,g-28)
    c: Horizontal(g14)
    c: Coincident(g15,g5)
    c: PointOnObject(g15,g-28)
    c: Horizontal(g15)
    c: Coincident(g16,g-15)
    c: PointOnObject(g16,g-22)
    c: Vertical(g16)
    c: PointOnObject(g17,g-24)
    c: Coincident(g17,g15)
    c: Vertical(g17)
    c: Coincident(g18,g15)
    c: PointOnObject(g18,g-34)
    c: Horizontal(g18)
    c: Coincident(g19,g18)
    c: PointOnObject(g19,g-34)
    c: Coincident(g20,g19)
    c: Coincident(g20,g14)
    c: Horizontal(g20)
    c: Coincident(g21,g14)
    c: Coincident(g21,g-28)
    c: PointOnObject(g22,g-24)
    c: Coincident(g23,g22)
    c: Vertical(g23)
    c: Coincident(g24,g23)
    c: PointOnObject(g24,g-33)
    c: Horizontal(g24)
    c: PointOnObject(g22,g-24)
    c: PointOnObject(g-20,g24)
    c: Equal(g24,g22)
    c: Equal(g22,g19)
    c: Coincident(g25,g-28)
    c: Horizontal(g25)
    c: Coincident(g26,g25)
    c: Coincident(g26,g22)
    c: Vertical(g26)
    c: Coincident(g27,g12)
    c: PointOnObject(g27,g-26)
    c: Vertical(g27)
    c: PointOnObject(g28,g-26)
    c: Coincident(g28,g9)
    c: Vertical(g28)
    c: Coincident(g29,g25)
    c: PointOnObject(g29,g-25)
    c: Vertical(g29)
    c: Coincident(g30,g23)
    c: PointOnObject(g30,g-25)
    c: Vertical(g30)
    c: Coincident(g31,g-30)
    c: PointOnObject(g31,g28)
    c: Horizontal(g31)
    c: Coincident(g32,g31)
    c: Coincident(g32,g28)
    c: Coincident(g33,g28)
    c: Coincident(g33,g27)
    c: PointOnObject(g34,g27)
    c: Coincident(g34,g27)
    c: Equal(g34,g32)
    c: Coincident(g35,g34)
    c: PointOnObject(g35,g-32)
    c: Horizontal(g35)
    c: Coincident(g36,g-29)
    c: PointOnObject(g36,g29)
    c: Horizontal(g36)
    c: Coincident(g37,g36)
    c: Coincident(g37,g29)
    c: Coincident(g38,g29)
    c: Coincident(g38,g30)
    c: PointOnObject(g39,g-33)
    c: PointOnObject(g39,g30)
    c: Horizontal(g39)
    c: Coincident(g40,g39)
    c: Coincident(g40,g30)
    c: Equal(g37,g40)
    c: PointOnObject(g41,g-26)
    c: PointOnObject(g41,g-30)
    c: Vertical(g41)
    c: Coincident(g42,g41)
    c: Horizontal(g42)
    c: Coincident(g43,g42)
    c: PointOnObject(g43,g-35)
    c: Vertical(g43)
    c: Coincident(g44,g43)
    c: PointOnObject(g44,g-30)
    c: Horizontal(g44)
    c: Coincident(g45,g44)
    c: Coincident(g45,g-30)
    c: Equal(g31,g41)
    c: Equal(g43,g41)
    c: Coincident(g46,g42)
    c: PointOnObject(g46,g-36)
    c: Horizontal(g46)
    c: Coincident(g47,g43)
    c: PointOnObject(g47,g-36)
    c: Horizontal(g47)
    c: PointOnObject(g48,g-25)
    c: PointOnObject(g48,g-29)
    c: Vertical(g48)
    c: Coincident(g49,g48)
    c: Coincident(g49,g46)
    c: Horizontal(g49)
    c: Coincident(g50,g46)
    c: Coincident(g50,g47)
    c: Coincident(g51,g47)
    c: PointOnObject(g51,g-29)
    c: Horizontal(g51)
    c: Coincident(g52,g51)
    c: Coincident(g52,g-29)
    c: PointOnObject(g53,g-32)
    c: PointOnObject(g53,g-33)
    c: Horizontal(g53)
    c: PointOnObject(g54,g-32)
    c: PointOnObject(g54,g-33)
    c: Horizontal(g54)
    c: PointOnObject(g55,g-32)
    c: PointOnObject(g55,g-33)
    c: Horizontal(g55)
    c: PointOnObject(g56,g-32)
    c: PointOnObject(g56,g-33)
    c: Horizontal(g56)
    c: PointOnObject(g-3,g53)
    c: PointOnObject(g-4,g54)
    c: PointOnObject(g-5,g55)
    c: PointOnObject(g-6,g56)
    c: Coincident(g58,g8)
    c: Coincident(g58,g0)
    c: Coincident(g59,g57)
    c: Coincident(g59,g57)
    c: Vertical(g59)
    c: Coincident(g60,g57)
    c: PointOnObject(g60,g1)
    c: Horizontal(g60)
    c: Coincident(g61,g60)
    c: Coincident(g61,g1)
    c: Coincident(g57,g0)
    c: Coincident(g62,g1)
    c: Coincident(g62,g2)
    c: Coincident(g63,g2)
    c: PointOnObject(g63,g2)
    c: Coincident(g64,g63)
    c: PointOnObject(g64,g16)
    c: Horizontal(g64)
    c: Coincident(g65,g64)
    c: Coincident(g65,g16)
    c: Coincident(g66,g16)
    c: Coincident(g66,g21)
    c: PointOnObject(g64,g-37)
    c: PointOnObject(g60,g-37)
    c: Coincident(g67,g-18)
    c: PointOnObject(g67,g-21)
    c: Vertical(g67)
    c: Coincident(g68,g-17)
    c: PointOnObject(g68,g-21)
    c: Vertical(g68)
    c: Coincident(g69,g-16)
    c: PointOnObject(g69,g-21)
    c: Vertical(g69)
    c: Coincident(g70,g-15)
    c: PointOnObject(g70,g-21)
    c: Vertical(g70)
    c: Coincident(g71,g45)
    c: Coincident(g71,g67)
    c: Coincident(g72,g68)
    c: Coincident(g72,g69)
    c: Coincident(g73,g70)
    c: Coincident(g73,g52)
    c: Coincident(g75,g74)
    c: Coincident(g75,g74)
    c: Vertical(g75)
    c: Coincident(g74,g67)
    c: PointOnObject(g74,g-38)
    c: Coincident(g76,g74)
    c: PointOnObject(g76,g68)
    c: Horizontal(g76)
    c: Coincident(g77,g76)
    c: Coincident(g77,g68)
    c: Coincident(g78,g69)
    c: PointOnObject(g78,g-38)
    c: Vertical(g78)
    c: Coincident(g79,g78)
    c: PointOnObject(g79,g-38)
    c: Coincident(g80,g79)
    c: Coincident(g80,g70)
    c: Vertical(g80)
    c: Coincident(g81,g35)
    c: Coincident(g81,g56)
    c: Coincident(g82,g56)
    c: PointOnObject(g82,g-19)
    c: Horizontal(g82)
    c: Coincident(g83,g82)
    c: PointOnObject(g83,g-19)
    c: Coincident(g84,g83)
    c: Coincident(g84,g55)
    c: Horizontal(g84)
    c: Coincident(g85,g55)
    c: Coincident(g85,g54)
    c: Coincident(g86,g54)
    c: PointOnObject(g86,g-19)
    c: Horizontal(g86)
    c: Coincident(g87,g86)
    c: PointOnObject(g87,g-19)
    c: Coincident(g88,g87)
    c: Coincident(g88,g53)
    c: Horizontal(g88)
    c: Coincident(g89,g53)
    c: Coincident(g89,g13)
    c: Coincident(g90,g39)
    c: Coincident(g90,g56)
    c: Coincident(g91,g56)
    c: PointOnObject(g91,g56)
    c: Coincident(g92,g91)
    c: PointOnObject(g92,g-20)
    c: Vertical(g92)
    c: Coincident(g93,g92)
    c: Coincident(g93,g55)
    c: Coincident(g94,g55)
    c: Coincident(g94,g54)
    c: Horizontal(g93)
    c: Coincident(g95,g24)
    c: Coincident(g95,g53)
    c: Coincident(g96,g53)
    c: PointOnObject(g96,g-20)
    c: Horizontal(g96)
    c: Coincident(g97,g96)
    c: PointOnObject(g97,g-20)
    c: Coincident(g98,g97)
    c: Coincident(g98,g54)
FEATURE [Sketcher::SketchObject] Sketch006  label="CUT-ROOF"
  ArcFitTolerance = 0
  ExternalGeometry = -> [Sketch004,Sketch002,Sketch001]
  FullyConstrained = true
  MakeInternals = false
  MapMode = 2
  sketch-geometry (49):
    g0: LineSegment [constr] StartX=107.1 StartY=188.836 StartZ=0 EndX=107.1 EndY=44.8363 EndZ=0
    g1: LineSegment [constr] StartX=134.7 StartY=188.836 StartZ=0 EndX=134.7 EndY=44.8363 EndZ=0
    g2: LineSegment [constr] StartX=162.3 StartY=188.836 StartZ=0 EndX=162.3 EndY=44.8363 EndZ=0
    g3: LineSegment [constr] StartX=189.9 StartY=188.836 StartZ=0 EndX=189.9 EndY=44.8363 EndZ=0
    g4: LineSegment [constr] StartX=247.5 StartY=366.836 StartZ=0 EndX=395.5 EndY=218.836 EndZ=0
    g5: LineSegment [constr] StartX=395.5 StartY=218.836 StartZ=0 EndX=247.5 EndY=218.836 EndZ=0
    g6: LineSegment [constr] StartX=247.5 StartY=244.145 StartZ=0 EndX=370.192 EndY=244.145 EndZ=0
    g7: LineSegment [constr] StartX=247.5 StartY=274.818 StartZ=0 EndX=339.519 EndY=274.818 EndZ=0
    g8: LineSegment [constr] StartX=247.5 StartY=305.49 StartZ=0 EndX=308.846 EndY=305.49 EndZ=0
    g9: LineSegment [constr] StartX=247.5 StartY=336.163 StartZ=0 EndX=278.173 EndY=336.163 EndZ=0
    g10: LineSegment [constr] StartX=217.5 StartY=44.8363 StartZ=0 EndX=395.5 EndY=44.8363 EndZ=0
    g11: LineSegment [constr] StartX=395.5 StartY=44.8363 StartZ=0 EndX=395.5 EndY=218.836 EndZ=0
    g12: LineSegment [constr] StartX=395.5 StartY=44.8363 StartZ=0 EndX=247.5 EndY=192.836 EndZ=0
    g13: LineSegment [constr] StartX=278.173 StartY=336.163 StartZ=0 EndX=278.173 EndY=162.163 EndZ=0
    g14: LineSegment [constr] StartX=308.846 StartY=305.49 StartZ=0 EndX=308.846 EndY=131.49 EndZ=0
    g15: LineSegment [constr] StartX=339.519 StartY=274.818 StartZ=0 EndX=339.519 EndY=100.818 EndZ=0
    g16: LineSegment [constr] StartX=370.192 StartY=244.145 StartZ=0 EndX=370.192 EndY=70.1447 EndZ=0
    g17: LineSegment [constr] StartX=278.173 StartY=162.163 StartZ=0 EndX=79.5 EndY=162.163 EndZ=0
    g18: LineSegment [constr] StartX=308.846 StartY=131.49 StartZ=0 EndX=79.5 EndY=131.49 EndZ=0
    g19: LineSegment [constr] StartX=370.192 StartY=70.1447 StartZ=0 EndX=79.5 EndY=70.1447 EndZ=0
    g20: LineSegment StartX=213.5 StartY=188.836 StartZ=0 EndX=213.5 EndY=162.163 EndZ=0
    g21: LineSegment StartX=217.5 StartY=162.163 StartZ=0 EndX=213.5 EndY=162.163 EndZ=0
    g22: LineSegment StartX=217.5 StartY=162.163 StartZ=0 EndX=217.5 EndY=131.49 EndZ=0
    g23: LineSegment StartX=217.5 StartY=131.49 StartZ=0 EndX=213.5 EndY=131.49 EndZ=0
    g24: LineSegment [constr] StartX=339.519 StartY=100.818 StartZ=0 EndX=217.5 EndY=100.818 EndZ=0
    g25: LineSegment StartX=213.5 StartY=131.49 StartZ=0 EndX=213.5 EndY=100.818 EndZ=0
    g26: LineSegment StartX=213.5 StartY=100.818 StartZ=0 EndX=217.5 EndY=100.818 EndZ=0
    g27: LineSegment StartX=217.5 StartY=100.818 StartZ=0 EndX=217.5 EndY=70.1447 EndZ=0
    g28: LineSegment StartX=217.5 StartY=70.1447 StartZ=0 EndX=213.5 EndY=70.1447 EndZ=0
    g29: LineSegment StartX=213.5 StartY=70.1447 StartZ=0 EndX=213.5 EndY=48.8363 EndZ=0
    g30: LineSegment StartX=83.5 StartY=188.836 StartZ=0 EndX=83.5 EndY=162.163 EndZ=0
    g31: LineSegment StartX=83.5 StartY=162.163 StartZ=0 EndX=79.5 EndY=162.163 EndZ=0
    g32: LineSegment StartX=79.5 StartY=162.163 StartZ=0 EndX=79.5 EndY=131.49 EndZ=0
    g33: LineSegment StartX=79.5 StartY=131.49 StartZ=0 EndX=83.5 EndY=131.49 EndZ=0
    g34: LineSegment StartX=83.5 StartY=131.49 StartZ=0 EndX=83.5 EndY=100.818 EndZ=0
    g35: LineSegment StartX=83.5 StartY=100.818 StartZ=0 EndX=79.5 EndY=100.818 EndZ=0
    g36: LineSegment StartX=79.5 StartY=100.818 StartZ=0 EndX=79.5 EndY=70.1447 EndZ=0
    g37: LineSegment StartX=79.5 StartY=70.1447 StartZ=0 EndX=83.5 EndY=70.1447 EndZ=0
    g38: LineSegment StartX=83.5 StartY=70.1447 StartZ=0 EndX=83.5 EndY=48.8363 EndZ=0
    g39: LineSegment StartX=83.5 StartY=48.8363 StartZ=0 EndX=107.1 EndY=48.8363 EndZ=0
    g40: LineSegment StartX=107.1 StartY=48.8363 StartZ=0 EndX=107.1 EndY=44.8363 EndZ=0
    g41: LineSegment StartX=107.1 StartY=44.8363 StartZ=0 EndX=134.7 EndY=44.8363 EndZ=0
    g42: LineSegment StartX=162.3 StartY=44.8363 StartZ=0 EndX=189.9 EndY=44.8363 EndZ=0
    g43: LineSegment StartX=213.5 StartY=48.8363 StartZ=0 EndX=189.9 EndY=48.8363 EndZ=0
    g44: LineSegment StartX=189.9 StartY=48.8363 StartZ=0 EndX=189.9 EndY=44.8363 EndZ=0
    g45: LineSegment StartX=162.3 StartY=44.8363 StartZ=0 EndX=162.3 EndY=48.8363 EndZ=0
    g46: LineSegment StartX=162.3 StartY=48.8363 StartZ=0 EndX=134.7 EndY=48.8363 EndZ=0
    g47: LineSegment StartX=134.7 StartY=48.8363 StartZ=0 EndX=134.7 EndY=44.8363 EndZ=0
    g48: LineSegment [constr] StartX=217.5 StartY=100.818 StartZ=0 EndX=79.5 EndY=100.818 EndZ=0
  constraints (136):
    c: Coincident(g0,g-3)
    c: PointOnObject(g0,g-13)
    c: Vertical(g0)
    c: PointOnObject(g1,g-13)
    c: Vertical(g1)
    c: Coincident(g2,g-20)
    c: PointOnObject(g2,g-13)
    c: Vertical(g2)
    c: Coincident(g3,g-21)
    c: PointOnObject(g3,g-13)
    c: Vertical(g3)
    c: Coincident(g1,g-19)
    c: Coincident(g4,g-23)
    c: Coincident(g5,g4)
    c: Coincident(g5,g-23)
    c: Horizontal(g5)
    c: Angle(g4,g5) = 0.785398
    c: Coincident(g6,g-27)
    c: PointOnObject(g6,g4)
    c: Horizontal(g6)
    c: Coincident(g7,g-26)
    c: PointOnObject(g7,g4)
    c: Horizontal(g7)
    c: Coincident(g8,g-25)
    c: PointOnObject(g8,g4)
    c: Horizontal(g8)
    c: Coincident(g9,g-24)
    c: PointOnObject(g9,g4)
    c: Horizontal(g9)
    c: Coincident(g10,g-28)
    c: Horizontal(g10)
    c: Coincident(g11,g10)
    c: Coincident(g11,g4)
    c: Vertical(g11)
    c: Coincident(g12,g10)
    c: Angle(g12,g10) = 0.785398
    c: Horizontal(g12,g-21)
    c: Coincident(g13,g9)
    c: PointOnObject(g13,g12)
    c: Vertical(g13)
    c: Coincident(g14,g8)
    c: PointOnObject(g14,g12)
    c: Vertical(g14)
    c: Coincident(g15,g7)
    c: PointOnObject(g15,g12)
    c: Vertical(g15)
    c: Coincident(g16,g6)
    c: PointOnObject(g16,g12)
    c: Vertical(g16)
    c: Coincident(g17,g13)
    c: PointOnObject(g17,g-16)
    c: Horizontal(g17)
    c: Coincident(g18,g14)
    c: PointOnObject(g18,g-16)
    c: Horizontal(g18)
    c: Coincident(g19,g16)
    c: PointOnObject(g19,g-16)
    c: Horizontal(g19)
    c: Coincident(g20,g-17)
    c: PointOnObject(g20,g17)
    c: Vertical(g20)
    c: PointOnObject(g21,g17)
    c: Coincident(g21,g20)
    c: Coincident(g22,g21)
    c: PointOnObject(g22,g18)
    c: Vertical(g22)
    c: Coincident(g23,g22)
    c: PointOnObject(g23,g18)
    c: PointOnObject(g22,g-18)
    c: PointOnObject(g23,g-17)
    c: Coincident(g24,g15)
    c: PointOnObject(g24,g-18)
    c: Horizontal(g24)
    c: Coincident(g25,g23)
    c: PointOnObject(g25,g-17)
    c: Coincident(g26,g25)
    c: Coincident(g26,g24)
    c: Horizontal(g26)
    c: Coincident(g27,g24)
    c: PointOnObject(g27,g-18)
    c: Coincident(g28,g27)
    c: PointOnObject(g28,g-17)
    c: Horizontal(g28)
    c: Coincident(g29,g28)
    c: PointOnObject(g29,g-17)
    c: PointOnObject(g28,g19)
    c: PointOnObject(g29,g-14)
    c: Coincident(g30,g-15)
    c: PointOnObject(g30,g17)
    c: Vertical(g30)
    c: Coincident(g31,g30)
    c: Coincident(g31,g17)
    c: Coincident(g32,g17)
    c: Coincident(g32,g18)
    c: Coincident(g33,g18)
    c: PointOnObject(g33,g-15)
    c: Horizontal(g33)
    c: Coincident(g34,g33)
    c: PointOnObject(g34,g-15)
    c: Coincident(g35,g34)
    c: PointOnObject(g35,g-16)
    c: Horizontal(g35)
    c: Coincident(g36,g35)
    c: Coincident(g36,g19)
    c: Coincident(g37,g19)
    c: PointOnObject(g37,g19)
    c: Coincident(g38,g37)
    c: PointOnObject(g38,g-14)
    c: Vertical(g38)
    c: Coincident(g39,g38)
    c: PointOnObject(g39,g0)
    c: Horizontal(g39)
    c: Coincident(g40,g39)
    c: Coincident(g40,g0)
    c: Coincident(g41,g0)
    c: Coincident(g41,g1)
    c: Coincident(g42,g2)
    c: Coincident(g42,g3)
    c: Coincident(g43,g29)
    c: PointOnObject(g43,g3)
    c: Horizontal(g43)
    c: Coincident(g44,g43)
    c: Coincident(g44,g3)
    c: Coincident(g45,g2)
    c: PointOnObject(g45,g-14)
    c: Vertical(g45)
    c: Coincident(g46,g45)
    c: PointOnObject(g46,g1)
    c: Horizontal(g46)
    c: Coincident(g47,g46)
    c: Coincident(g47,g1)
    c: PointOnObject(g38,g-15)
    c: Coincident(g48,g24)
    c: PointOnObject(g48,g-16)
    c: Horizontal(g48)
    c: PointOnObject(g35,g48)
FEATURE [Part::Part2DObjectPython] Clone2D002  label="Model-CUT-BOX-WALLS"  # Draft 2D object (typed FeaturePython)
  Fuse = false
  Objects = -> [Sketch004]
  PathResource = Model
  Scale = (1,1,1)
FEATURE [Part::Part2DObjectPython] Clone2D003  label="Model-CUT-BOX-WALS2"  # Draft 2D object (typed FeaturePython)
  Fuse = false
  PathResource = Model
  Scale = (1,1,1)
FEATURE [Part::Part2DObjectPython] Clone2D004  label="Model-CUT-ROOF"  # Draft 2D object (typed FeaturePython)
  Fuse = false
  Objects = -> [Sketch006]
  PathResource = Model
  Scale = (1,1,1)
FEATURE [App::DocumentObjectGroup] Model
  Group = -> [Clone2D,Clone2D001,Clone2D002,Clone2D003,Clone2D004]
FEATURE [Path::FeaturePython] Job  # Path/CAM operation (typed FeaturePython)
  CycleTime = 00:00:04
  Fixtures = G54
  GeometryTolerance = 0.01
  JobType = 0
  Model = -> Model
  Operations = -> Operations
  OrderOutputBy = 0
  PostProcessor = 10
  PostProcessorOutputFile = <userpath>/Documents/AdruinoAtariPaddle/FREECAD/HousingAtari_RAW.nc
  SetupSheet = -> SetupSheet
  SplitOutput = false
  Stock = -> Stock001
  Tools = -> Tools
FEATURE [Sketcher::SketchObject] Sketch007
  ArcFitTolerance = 1e-06
  AttachmentSupport = -> [Sketch006]
  ExternalGeometry = -> [Sketch006]
  FullyConstrained = true
  MakeInternals = false
  MapMode = 2
  sketch-geometry (4):
    g0: LineSegment StartX=93.5 StartY=178.836 StartZ=0 EndX=93.5 EndY=60.1447 EndZ=0
    g1: LineSegment StartX=93.5 StartY=60.1447 StartZ=0 EndX=203.5 EndY=60.1447 EndZ=0
    g2: LineSegment StartX=203.5 StartY=60.1447 StartZ=0 EndX=203.5 EndY=178.836 EndZ=0
    g3: LineSegment StartX=203.5 StartY=178.836 StartZ=0 EndX=93.5 EndY=178.836 EndZ=0
  constraints (12):
    c: Coincident(g0,g1)
    c: Coincident(g1,g2)
    c: Coincident(g2,g3)
    c: Coincident(g3,g0)
    c: Vertical(g0)
    c: Vertical(g2)
    c: Horizontal(g1)
    c: Horizontal(g3)
    c: DistanceX(g1,g-5) = 10
    c: DistanceY(g1,g-5) = 10
    c: DistanceX(g-3,g0) = 10
    c: DistanceY(g0,g-3) = 10
note: 1 file-system path scrubbed to <path> (originals preserved in the JSON sidecar)
